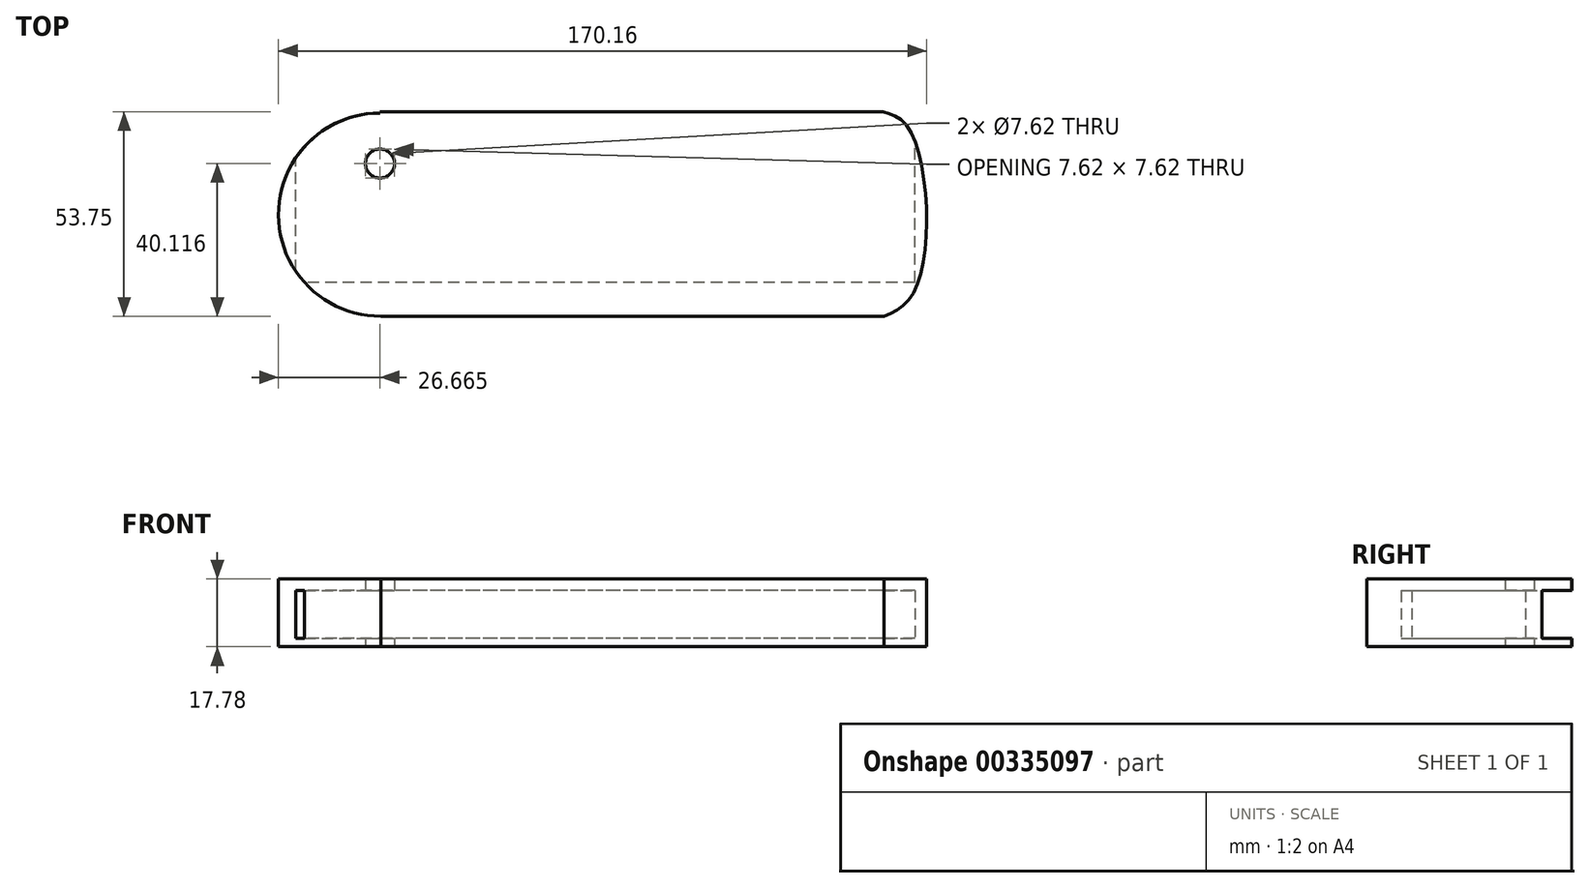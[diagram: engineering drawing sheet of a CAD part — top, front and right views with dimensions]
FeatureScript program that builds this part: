
annotation { "Feature Type Name" : "Feature", "Feature Type Description" : "" }
export const myFeature = defineFeature(function(context is Context, id is Id, definition is map)
    precondition{}
    {
        {
            var Q0;
            Q0=qCreatedBy(makeId("Top.planeOp"),FACE);
            var sketch = newSketch(context, id + "F0", { "sketchPlane" : qUnion([Q0])});
            skLineSegment(sketch, "E0", {"start": v(-52, 27.04) * mm, "end": v(80.07, 27.04) * mm});
            skLineSegment(sketch, "E1", {"start": v(-51.74, -26.71) * mm, "end": v(80.34, -26.71) * mm});
            skFitSpline(sketch, "E2", {"points": [v(80.07, 27.04) * mm, v(86.25, 23.44) * mm, v(91.47, 0) * mm, v(87.3, -21.73) * mm, v(80.34, -26.71) * mm], "startDerivative": vector(37.57, -10.96) * mm, "endDerivative": vector(-39.58, -17.72) * mm});
            skArc(sketch, "E3", {"start": v(-52, 26.67) * mm, "mid": v(-78.67, -0.13) * mm, "end": v(-51.74, -26.66) * mm});
            skLineSegment(sketch, "E4", {"start": v(-52, 27.04) * mm, "end": v(-52, 26.67) * mm});
            skLineSegment(sketch, "E5.trimOffspring", {"start": v(-51.74, -26.66) * mm, "end": v(-51.74, -26.71) * mm});
            skCircle(sketch, "E6", {"center": v(-52, 13.4) * mm, "radius": 3.81 * mm});
            skSolve(sketch);
        }
        {
            var Q0;
            Q0 = qSketchRegion(id + "F0", true);
            extrude(context, id + "F1", {"entities" : qUnion([Q0]), "depth" : 17.78 * mm});
        }
        {
            var Q0;
            Q0=qCreatedBy(makeId("Front.planeOp"),FACE);
            cPlane(context, id + "F2", {"entities" : qUnion([Q0]), "cplaneType" : CPlaneType.OFFSET, "offset" : 27.18 * mm, "oppositeDirection" : true, "width" : 152.4 * mm, "height" : 152.4 * mm});
        }
        {
            var Q0;
            Q0=qCreatedBy(id+"F2.planeOp",FACE);
            var sketch = newSketch(context, id + "F3", { "sketchPlane" : qUnion([Q0])});
            skLineSegment(sketch, "E7.bottom", {"start": v(88.44, 14.7) * mm, "end": v(-74.12, 14.7) * mm});
            skLineSegment(sketch, "E7.top", {"start": v(88.44, 2.22) * mm, "end": v(-74.12, 2.22) * mm});
            skLineSegment(sketch, "E7.left", {"start": v(88.44, 14.7) * mm, "end": v(88.44, 2.22) * mm});
            skLineSegment(sketch, "E7.right", {"start": v(-74.12, 14.7) * mm, "end": v(-74.12, 2.22) * mm});
            skSolve(sketch);
        }
        {
            var Q0;
            Q0=makeQuery(id+"F3.imprint","IMPRINT",FACE,{"disambiguationData":[TD([[makeQuery(id+"F3.imprint","IMPRINT",EDGE,{"derivedFrom":sQuery(id+"F3.wireOp",EDGE,"E7.bottom")}),1.0]])]});
            extrude(context, id + "F4", {"entities" : qUnion([Q0]), "operationType" : NewBodyOperationType.REMOVE, "depth" : 44.96 * mm});
        }
    });
